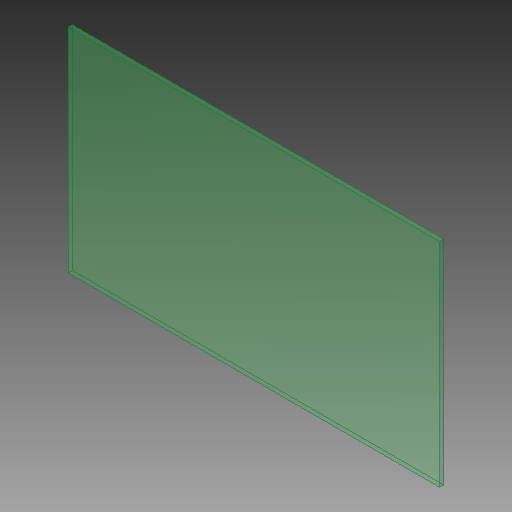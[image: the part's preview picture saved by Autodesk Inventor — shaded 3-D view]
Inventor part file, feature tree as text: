
AUTODESK INVENTOR PART (.ipt)
format: ipt  version: 2018.1 (Build 221171000, 171)  size: 132,608 bytes
history: native  units: mm
features: extrude x2, sketch x2
ambient origin geometry x8: Origin, YZ Plane, XZ Plane, XY Plane, X Axis, Y Axis, Z Axis, Center Point
bodies: Solid1 (feature_tree)
feature tree (4):
  extrude  "Extrusion1"  Depth=258.0mm
  extrude  "Extrusion2"  TaperAngle=0.0deg  [1 undecoded]
  sketch  "Sketch1"  dims[d0=450.0mm d1=258.0mm]
  sketch  "Sketch2"  dims[d2=5.0mm d3=0.0mm d4=39.0mm d5=29.5mm d6=119.5mm d7=39.0mm d8=25.0mm d9=25.0mm d10=48.0mm d11=36.0mm d12=25.0mm d13=25.0mm d14=29.5mm d15=29.5mm d16=29.5mm d17=144.0mm d18=144.0mm d19=144.0mm d20=144.0mm d21=82.0mm d22=100.0mm d23=75.0mm d24=34.0mm d25=62.0mm d26=50.5mm d27=45.0mm d28=32.0mm d29=25.0mm d30=16.0mm d31=16.0mm d32=28.0mm d33=28.0mm d34=16.0mm d35=16.0mm d36=5.0mm d37=0.0mm]
note: 1 required parameter value undecoded (feature->parameter linkage not recoverable at this tier; creation-order binding heuristic only, values carry confidence <= 0.55)
